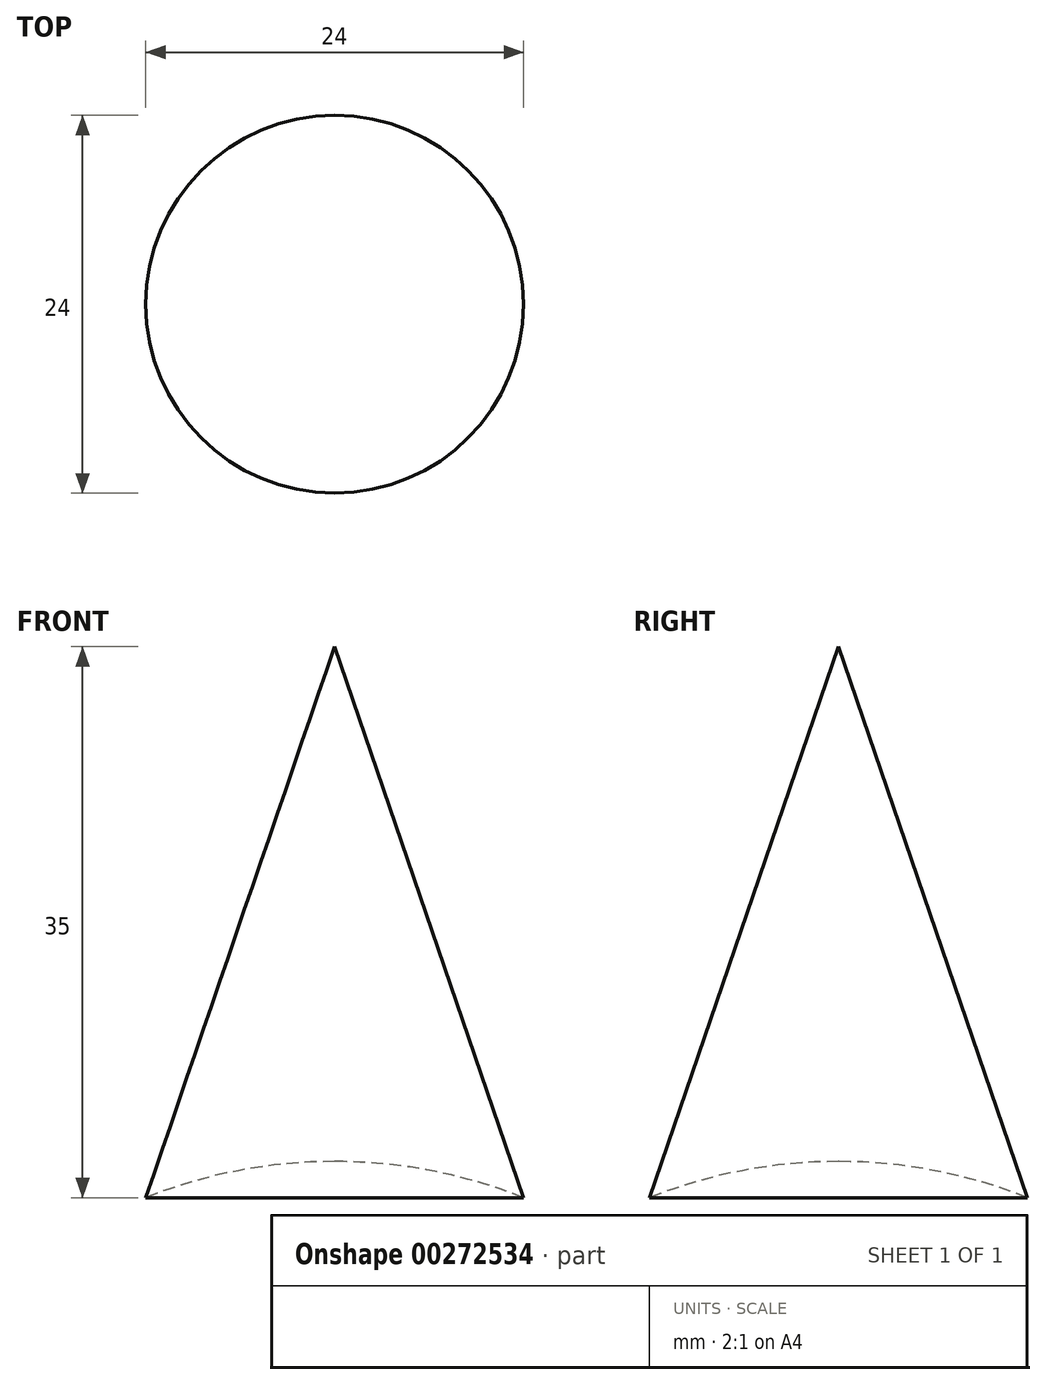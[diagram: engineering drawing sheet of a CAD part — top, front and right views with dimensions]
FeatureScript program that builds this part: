
annotation { "Feature Type Name" : "Feature", "Feature Type Description" : "" }
export const myFeature = defineFeature(function(context is Context, id is Id, definition is map)
    precondition{}
    {
        {
            var Q0;
            Q0=qCreatedBy(makeId("Front.planeOp"),FACE);
            var sketch = newSketch(context, id + "F0", { "sketchPlane" : qUnion([Q0])});
            skLineSegment(sketch, "E0", {"start": v(0, 0) * mm, "end": v(0, 35) * mm});
            skLineSegment(sketch, "E1", {"start": v(0, 35) * mm, "end": v(12, 0) * mm});
            skLineSegment(sketch, "E2", {"start": v(12, 0) * mm, "end": v(0, 0) * mm});
            skSolve(sketch);
        }
        {
            var Q0;
            Q0 = qSketchRegion(id + "F0", true);
            var Q1;
            Q1=sQuery(id+"F0.wireOp",EDGE,"E0");
            revolve(context, id + "F1", {"entities" : qUnion([Q0]), "axis" : qUnion([Q1]), "revolveType" : RevolveType.FULL});
        }
        {
            var Q0;
            Q0=qCreatedBy(makeId("Front.planeOp"),FACE);
            var sketch = newSketch(context, id + "F2", { "sketchPlane" : qUnion([Q0])});
            skLineSegment(sketch, "E3", {"start": v(-12, 0) * mm, "end": v(12, 0) * mm, "construction": true});
            skArc(sketch, "E4", {"start": v(12, 0) * mm, "mid": v(6.1, 1.72) * mm, "end": v(0, 2.3) * mm});
            skLineSegment(sketch, "E5", {"start": v(0, 0) * mm, "end": v(0, 2.3) * mm});
            skLineSegment(sketch, "E6", {"start": v(0, 0) * mm, "end": v(12, 0) * mm});
            skSolve(sketch);
        }
        {
            var Q0;
            Q0 = qSketchRegion(id + "F2", true);
            var Q1;
            Q1=sQuery(id+"F2.wireOp",EDGE,"E5");
            revolve(context, id + "F3", {"operationType" : NewBodyOperationType.REMOVE, "entities" : qUnion([Q0]), "axis" : qUnion([Q1]), "revolveType" : RevolveType.FULL, "oppositeDirection" : true});
        }
    });
